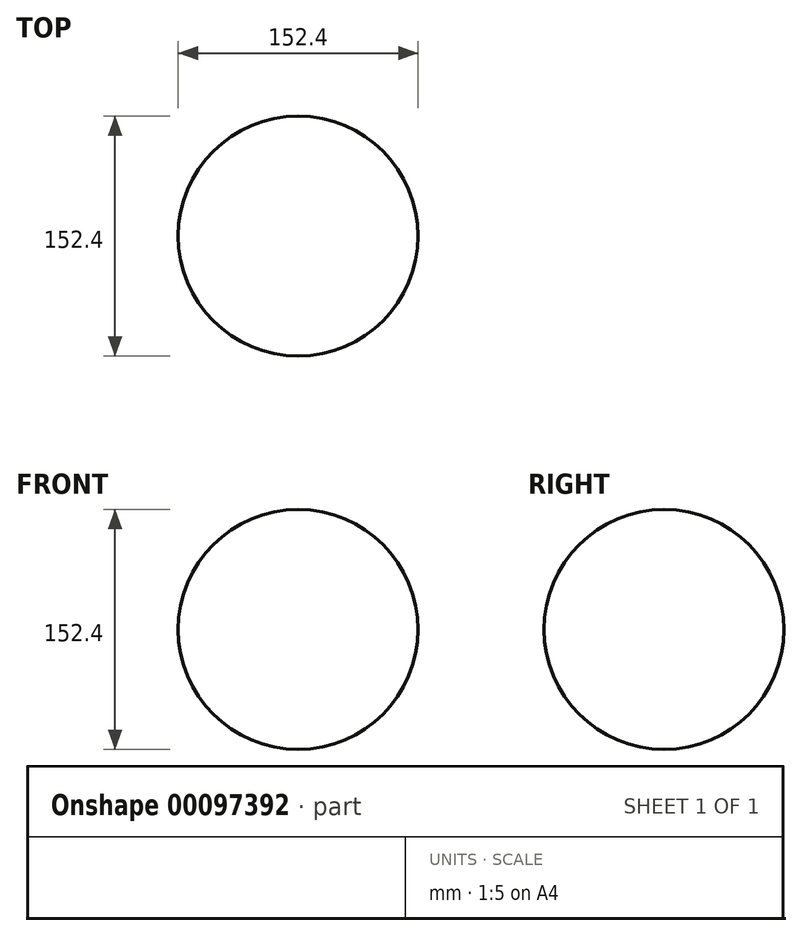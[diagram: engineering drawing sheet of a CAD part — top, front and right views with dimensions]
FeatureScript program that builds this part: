
annotation { "Feature Type Name" : "Feature", "Feature Type Description" : "" }
export const myFeature = defineFeature(function(context is Context, id is Id, definition is map)
    precondition{}
    {
        {
            var Q0;
            Q0=qCreatedBy(makeId("Top.planeOp"),FACE);
            var sketch = newSketch(context, id + "F0", { "sketchPlane" : qUnion([Q0])});
            skLineSegment(sketch, "E0", {"start": v(0, 0) * mm, "end": v(0, 152.4) * mm});
            skArc(sketch, "E1", {"start": v(0, 152.4) * mm, "mid": v(-76.2, 76.2) * mm, "end": v(0, 0) * mm});
            skSolve(sketch);
        }
        {
            var Q0;
            Q0=makeQuery(id+"F0.imprint","IMPRINT",FACE,{"disambiguationData":[TD([[makeQuery(id+"F0.imprint","IMPRINT",EDGE,{"derivedFrom":sQuery(id+"F0.wireOp",EDGE,"E0")}),1.0]])]});
            var Q1;
            Q1=sQuery(id+"F0.wireOp",EDGE,"E0");
            revolve(context, id + "F1", {"entities" : qUnion([Q0]), "axis" : qUnion([Q1]), "revolveType" : RevolveType.FULL});
        }
    });
